# Revit family: Plum Fix_Shower_Argent_Pallas Overhead showerhead
name_source: partatom
category: Plumbing Fixtures
revit_build: Autodesk Revit 2016 (Build: 20190508_0715(x64)
units: mm (PartAtom-declared; Revit-internal decimal feet)

## family parameters
Always vertical = Yes
Cut with Voids When Loaded = No
OmniClass Number = 23.45.05.14.17
OmniClass Title = Showers
Part Type = Normal
Room Calculation Point = No
Round Connector Dimension = Use Diameter
Shared = No
Work Plane-Based = No

## types (4) — shared parameters
CW Connection = No
Description = Pallas 230 Overhead shower
HW Connection = Yes
IfcExportAs = IfcSanitaryTerminal
IfcExportType = SHOWER
Manufacturer = Argent
Manufacturer_Overall Depth = 230 mm
Manufacturer_Overall Height = 60 mm
Manufacturer_Overall Width = 230 mm
Manufacturer_URL__Product Specific = https://www.argentaust.com.au
ModifiedIssue_ANZRS = 20200421 $
URL = https://www.argentaust.com.au
Uniclass2015Code = Pr_40_20_87_76
Uniclass2015Title = Shower heads
Uniclass2015Version = Products v1.17
Vent Connection = No
Waste Connection = No
zero-valued in all types: Cost

## per-type parameters (varying)
| type | Body Material | Manufacturer_Spec Code | Model | Type Comments |
| Chrome (OH112301) | z_Argent_Chrome | OH112301 | OH112301 | Chrome Finish |
| Brushed Nickel (OH112301BN) | z_Argent_Brushed Nickel | OH112301BN | OH112301BN | Brushed Nickel Finish |
| Matte Black (OH112301MB) | z_Argent_Matte Black | OH112301MB | OH112301MB | Matte Black Finish |
| Sunset (OH112301RG) | z_Argent_Sunset | OH112301RG | OH112301RG | Sunset Finish |

## geometry (parser evidence)
native form markers: Sweep x2
no freeform markers — native parametric forms only
